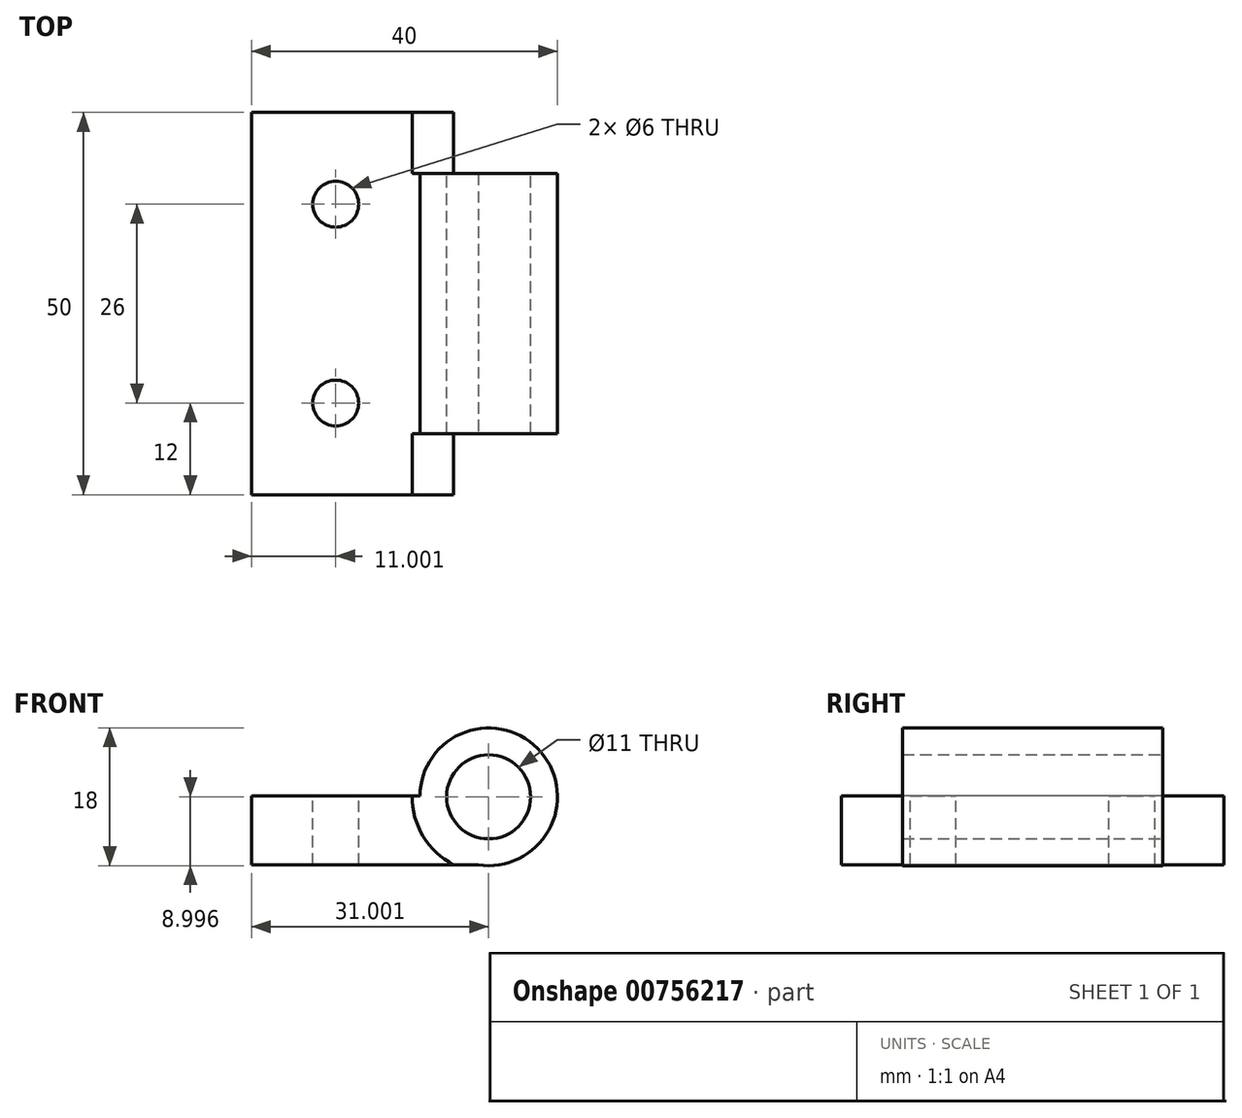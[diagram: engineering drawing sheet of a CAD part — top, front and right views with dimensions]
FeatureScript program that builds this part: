
annotation { "Feature Type Name" : "Feature", "Feature Type Description" : "" }
export const myFeature = defineFeature(function(context is Context, id is Id, definition is map)
    precondition{}
    {
        {
            var Q0;
            Q0=qCreatedBy(makeId("Front.planeOp"),FACE);
            var sketch = newSketch(context, id + "F0", { "sketchPlane" : qUnion([Q0])});
            skLineSegment(sketch, "E0", {"start": v(0, 0) * mm, "end": v(32.37, 0) * mm});
            skLineSegment(sketch, "E1", {"start": v(40, 8.8) * mm, "end": v(40, 9) * mm});
            skLineSegment(sketch, "E2", {"start": v(22, 9) * mm, "end": v(0, 9) * mm});
            skLineSegment(sketch, "E3", {"start": v(0, 9) * mm, "end": v(0, 0) * mm});
            skCircle(sketch, "E4", {"center": v(31, 8.9) * mm, "radius": 9 * mm});
            skPoint(sketch, "E4.second.point", {"position": v(29.64, 0) * mm});
            skPoint(sketch, "E4.third.point", {"position": v(22, 9) * mm});
            skLineSegment(sketch, "E5", {"start": v(0, -10.71) * mm, "end": v(40, -10.71) * mm, "construction": true});
            skLineSegment(sketch, "E6", {"start": v(40, -10.71) * mm, "end": v(40, 9) * mm, "construction": true});
            skLineSegment(sketch, "E7", {"start": v(0, -10.71) * mm, "end": v(0, 0) * mm, "construction": true});
            skSolve(sketch);
        }
        {
            var Q0;
            Q0=qSketchRegion(id+"F0",true);
            extrude(context, id + "F1", {"entities" : qUnion([Q0]), "oppositeDirection" : true, "depth" : 50 * mm, "offsetDistance" : 25 * mm});
        }
        {
            var Q0;
            Q0=makeQuery(id+"F1.opExtrude","SWEPT_FACE",FACE,{"disambiguationData":[OSD([sQuery(id+"F0.wireOp",EDGE,"E2")])]});
            var sketch = newSketch(context, id + "F2", { "sketchPlane" : qUnion([Q0])});
            skCircle(sketch, "E8", {"center": v(11, 38) * mm, "radius": 3 * mm});
            skPoint(sketch, "E8.centerSnap0", {"position": v(11, 50) * mm});
            skCircle(sketch, "E9", {"center": v(11, 12) * mm, "radius": 3 * mm});
            skSolve(sketch);
        }
        {
            var Q0;
            Q0=qSketchRegion(id+"F2",true);
            extrude(context, id + "F3", {"entities" : qUnion([Q0]), "operationType" : NewBodyOperationType.REMOVE, "oppositeDirection" : true, "depth" : 25 * mm, "offsetDistance" : 25 * mm});
        }
        {
            var Q0;
            Q0=makeQuery(id+"F1.opExtrude","CAP_FACE",FACE,{"disambiguationData":[OSD([sQuery(id+"F0.wireOp",EDGE,"E0"),sQuery(id+"F0.wireOp",EDGE,"E2"),sQuery(id+"F0.wireOp",EDGE,"E3"),sQuery(id+"F0.wireOp",EDGE,"E4")])],"isStart":true});
            cPlane(context, id + "F4", {"entities" : qUnion([Q0]), "cplaneType" : CPlaneType.OFFSET, "offset" : 7 * mm, "oppositeDirection" : true, "width" : 150 * mm, "height" : 150 * mm});
        }
        {
            var Q0;
            Q0=makeQuery(id+"F1.opExtrude","CAP_FACE",FACE,{"disambiguationData":[OSD([sQuery(id+"F0.wireOp",EDGE,"E0"),sQuery(id+"F0.wireOp",EDGE,"E2"),sQuery(id+"F0.wireOp",EDGE,"E3"),sQuery(id+"F0.wireOp",EDGE,"E4")])],"isStart":true});
            var sketch = newSketch(context, id + "F5", { "sketchPlane" : qUnion([Q0])});
            skCircle(sketch, "E10", {"center": v(31, 8.9) * mm, "radius": 10 * mm});
            skSolve(sketch);
        }
        {
            var Q0;
            Q0 = qSketchRegion(id + "F5", true);
            extrude(context, id + "F6", {"entities" : qUnion([Q0]), "operationType" : NewBodyOperationType.REMOVE, "oppositeDirection" : true, "depth" : 8 * mm, "offsetDistance" : 25 * mm});
        }
        {
            var Q0;
            Q0=makeQuery(id+"F1.opExtrude","CAP_FACE",FACE,{"disambiguationData":[OSD([sQuery(id+"F0.wireOp",EDGE,"E0"),sQuery(id+"F0.wireOp",EDGE,"E2"),sQuery(id+"F0.wireOp",EDGE,"E3"),sQuery(id+"F0.wireOp",EDGE,"E4")])],"isStart":false});
            var sketch = newSketch(context, id + "F7", { "sketchPlane" : qUnion([Q0])});
            skCircle(sketch, "E11", {"center": v(-31, 8.9) * mm, "radius": 10 * mm});
            skSolve(sketch);
        }
        {
            var Q0;
            Q0 = qSketchRegion(id + "F7", true);
            extrude(context, id + "F8", {"entities" : qUnion([Q0]), "operationType" : NewBodyOperationType.REMOVE, "oppositeDirection" : true, "depth" : 8 * mm, "offsetDistance" : 25 * mm});
        }
        {
            var Q0;
            Q0=makeQuery(id+"F8.boolean.opBoolean","COPY",FACE,{"derivedFrom":makeQuery(id+"F8.opExtrude","CAP_FACE",FACE,{"disambiguationData":[OSD([sQuery(id+"F7.wireOp",EDGE,"E11")])],"isStart":false})});
            var sketch = newSketch(context, id + "F9", { "sketchPlane" : qUnion([Q0])});
            skCircle(sketch, "E12", {"center": v(-31, 8.9) * mm, "radius": 5.5 * mm});
            skSolve(sketch);
        }
        {
            var Q0;
            Q0 = qSketchRegion(id + "F9", true);
            extrude(context, id + "F10", {"entities" : qUnion([Q0]), "operationType" : NewBodyOperationType.REMOVE, "endBound" : BoundingType.THROUGH_ALL, "oppositeDirection" : true, "depth" : 25 * mm, "offsetDistance" : 25 * mm});
        }
    });
